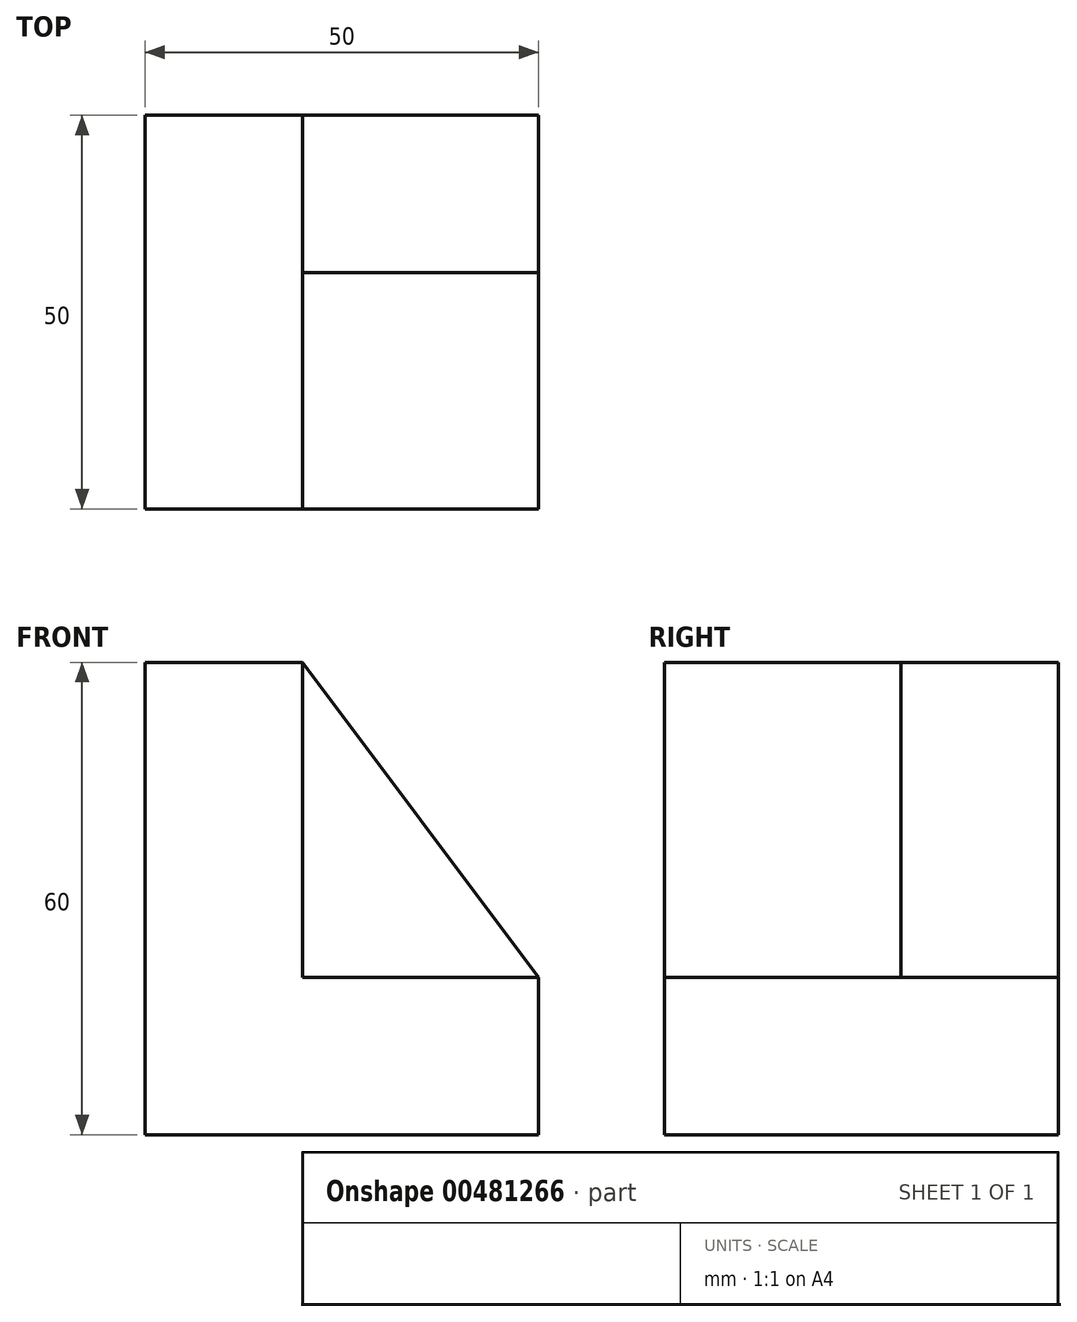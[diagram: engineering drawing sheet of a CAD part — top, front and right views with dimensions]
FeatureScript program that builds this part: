
annotation { "Feature Type Name" : "Feature", "Feature Type Description" : "" }
export const myFeature = defineFeature(function(context is Context, id is Id, definition is map)
    precondition{}
    {
        {
            var Q0;
            Q0=qCreatedBy(makeId("Front.planeOp"),FACE);
            var sketch = newSketch(context, id + "F0", { "sketchPlane" : qUnion([Q0])});
            skLineSegment(sketch, "E0", {"start": v(0, 0) * mm, "end": v(0, 60) * mm});
            skLineSegment(sketch, "E1", {"start": v(0, 60) * mm, "end": v(20, 60) * mm});
            skLineSegment(sketch, "E2", {"start": v(20, 60) * mm, "end": v(20, 20) * mm});
            skLineSegment(sketch, "E3", {"start": v(20, 20) * mm, "end": v(50, 20) * mm});
            skLineSegment(sketch, "E4", {"start": v(50, 20) * mm, "end": v(50, 0) * mm});
            skLineSegment(sketch, "E5", {"start": v(50, 0) * mm, "end": v(0, 0) * mm});
            skSolve(sketch);
        }
        {
            var Q0;
            Q0=makeQuery(id+"F0.imprint","IMPRINT",FACE,{"disambiguationData":[TD([[makeQuery(id+"F0.imprint","IMPRINT",EDGE,{"derivedFrom":sQuery(id+"F0.wireOp",EDGE,"E0")}),-1.0]])]});
            extrude(context, id + "F1", {"entities" : qUnion([Q0]), "depth" : 50 * mm});
        }
        {
            var Q0;
            Q0=makeQuery(id+"F1.opExtrude","CAP_FACE",FACE,{"disambiguationData":[OSD([sQuery(id+"F0.wireOp",EDGE,"E0"),sQuery(id+"F0.wireOp",EDGE,"E1"),sQuery(id+"F0.wireOp",EDGE,"E2"),sQuery(id+"F0.wireOp",EDGE,"E3"),sQuery(id+"F0.wireOp",EDGE,"E4"),sQuery(id+"F0.wireOp",EDGE,"E5")])],"isStart":true});
            var sketch = newSketch(context, id + "F2", { "sketchPlane" : qUnion([Q0])});
            skLineSegment(sketch, "E6", {"start": v(-20, 60) * mm, "end": v(-50, 20) * mm});
            skLineSegment(sketch, "E7", {"start": v(-50, 20) * mm, "end": v(-20, 20) * mm});
            skLineSegment(sketch, "E8", {"start": v(-20, 20) * mm, "end": v(-20, 60) * mm});
            skSolve(sketch);
        }
        {
            var Q0;
            Q0 = qSketchRegion(id + "F2", true);
            extrude(context, id + "F3", {"entities" : qUnion([Q0]), "operationType" : NewBodyOperationType.ADD, "oppositeDirection" : true, "depth" : 20 * mm});
        }
    });
